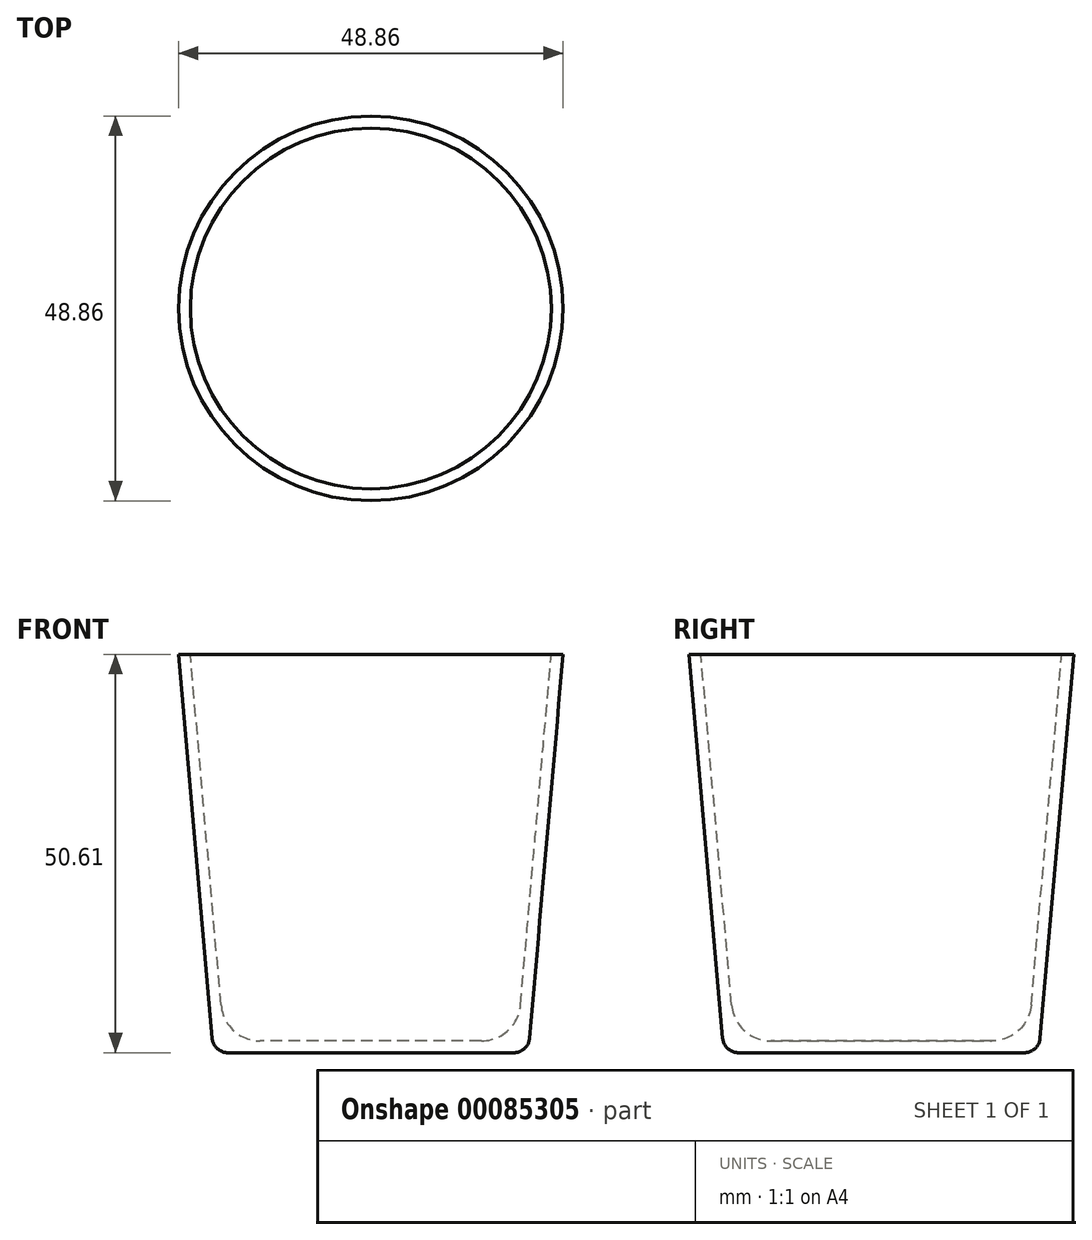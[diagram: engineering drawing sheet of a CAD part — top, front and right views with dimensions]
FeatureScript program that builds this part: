
annotation { "Feature Type Name" : "Feature", "Feature Type Description" : "" }
export const myFeature = defineFeature(function(context is Context, id is Id, definition is map)
    precondition{}
    {
        {
            var Q0;
            Q0=qCreatedBy(makeId("Front.planeOp"),FACE);
            var sketch = newSketch(context, id + "F0", { "sketchPlane" : qUnion([Q0])});
            skLineSegment(sketch, "E0", {"start": v(0, 0) * mm, "end": v(-20, 0) * mm});
            skLineSegment(sketch, "E1", {"start": v(-20, 0) * mm, "end": v(-24.43, 50.6) * mm});
            skLineSegment(sketch, "E2", {"start": v(-24.43, 50.6) * mm, "end": v(0, 50.6) * mm});
            skLineSegment(sketch, "E3", {"start": v(0, 50.6) * mm, "end": v(0, 0) * mm});
            skSolve(sketch);
        }
        {
            var Q0;
            Q0 = qSketchRegion(id + "F0", true);
            var Q1;
            Q1=sQuery(id+"F0.wireOp",EDGE,"E3");
            revolve(context, id + "F3", {"entities" : qUnion([Q0]), "axis" : qUnion([Q1]), "revolveType" : RevolveType.FULL});
        }
        {
            var Q0;
            Q0=makeQuery(id+"F3.opRevolve","SWEPT_FACE",FACE,{"disambiguationData":[OSD([sQuery(id+"F0.wireOp",EDGE,"E2")])]});
            shell(context, id + "F1", {"entities" : qUnion([Q0]), "thickness" : 1.5 * mm});
        }
        {
            var Q0;
            Q0=makeQuery(id+"F1.opShell","OFFSET_EDGE",EDGE,{"disambiguationData":[OSD([sQuery(id+"F0.wireOp",EDGE,"E0"),sQuery(id+"F0.wireOp",EDGE,"E1")])]});
            fillet(context, id + "F2", {"entities" : qUnion([Q0]), "radius" : 5 * mm, "tangentPropagation" : true, "allowEdgeOverflow" : false});
        }
        {
            var Q0;
            Q0=makeQuery(id+"F3.opRevolve","SWEPT_EDGE",EDGE,{"disambiguationData":[OSD([sQuery(id+"F0.wireOp",EDGE,"E0"),sQuery(id+"F0.wireOp",EDGE,"E1")])]});
            fillet(context, id + "F4", {"entities" : qUnion([Q0]), "radius" : 2 * mm, "tangentPropagation" : true, "allowEdgeOverflow" : false});
        }
    });
